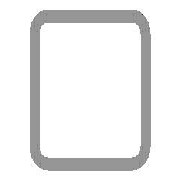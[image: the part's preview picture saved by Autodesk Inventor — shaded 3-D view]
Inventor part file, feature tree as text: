
AUTODESK INVENTOR PART (.ipt)
format: ipt  version: 2025.1 (Build 291241020, 241B)  size: 136,704 bytes
history: native  units: mm (DEFAULTED — no unit token found)
features: other x4, sketch x1, plane x1
ambient origin geometry x8: Origin, YZ Plane, XZ Plane, XY Plane, X Axis, Y Axis, Z Axis, Center Point
bodies: Solid1 (feature_tree), Body (feature_tree)
feature tree (6):
  parser-record x1  (decoder bookkeeping rows leaked as tree rows — omitted from the tree; the rows remain in map.json)
  other  "Driven Length"
  other  "Start Plane"
  other  "End Plane"
  sketch  "Sketch3"  dims[d3=1710.0mm d4=0.0mm d7=4.5mm d10=80.0mm d11=80.0mm d12=3.0mm d13=-0.0mm d14=1710.0mm d15=40.0mm d16=40.0mm d17=90.0deg d18=1710.0mm]
  plane  "Work Plane3"
